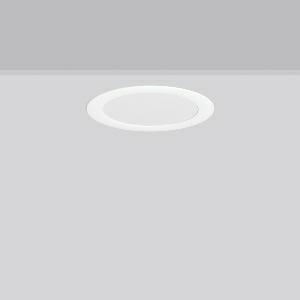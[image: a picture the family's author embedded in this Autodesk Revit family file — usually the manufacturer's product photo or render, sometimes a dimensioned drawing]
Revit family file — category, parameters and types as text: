
# Revit family: toledo_flat_round_e_672230_002_1_3b37
name_source: partatom
category: Lighting Fixtures
units: mm (PartAtom-declared; Revit-internal decimal feet)

## family parameters
Cut with Voids When Loaded = No
Host = Face
Light Source = No
Part Type = Normal
Room Calculation Point = No
Round Connector Dimension = Use Diameter
Shared = No

## types (1)
- TOLEDO FLAT round E (1 x LED Modul 840, 1800 lm, 4000)
    Apparent Load = 17 VA
    CIE Flux Codes = 48 79 96 100 100
    Color Rendering = 80
    Color Temperature = 4000
    Default Elevation = 1800 mm  [stored 5.90551 ft]
    Description = Series: TOLEDO FLAT round
Ultra thin recessed downlight. For escape route illumination. Housing: die-cast aluminium, powder-coated. Lightguide and diffuser made of non-yellowing plastic (PMMA). Diffuser opal matt plastic. Ceiling installation with spring system. Including separate LED converter with connecting cable 250 mm. Suitable for connection to central battery systems. External driver with simple plug-in locking system. 
Colour: white
Diameter: 255 mm
Height: 3 mm
Cut-out diameter: 234 mm
Recess height: 35 mm
Luminaire: recess height: 31-51 mm
Weight: 0.81 kg
Operating mode: maintained power mode
Lamp: LED
Socket: without socket
Colour temperature: 4000K
Colour rendering index (CRI): 80
System power: 17 W
Rated luminous flux: 1800 lm
Luminous flux, emergency: 1800 lm
System power, emergency: 17 W
Control gear: Regulated power supply
Protection class: II
Type of protection: IP 54
    Height = 0 mm  [stored 0 ft]
    Lamp = 1 x LED Modul 840
    Lamp Light Flux = 1800 lm
    Lamp count = 1
    Length = 255 mm
    Lifetime = 50000 h
    Luminous efficacy = 106 lm/W
    Manufacturer = RZB
    ModVariant = No
    Model = 672230.002.1
    Mounting Place = Ceiling
    Mounting Type = Recessed
    Number of Poles = 1
    OnlyDefault = Yes
    Power Factor = 1
    Product Name = TOLEDO FLAT round E
    Product group = Recessed downlights
    ProductGroupID = 402
    Protection Class = Protection class II
    Protection Degree = IP 40
    RLX_Detail_Level = 1
    RLX_Emergency_Light_Flux = 1800 lm
    RLX_Emergency_Type = 3
    RLX_Emergency_Type_DB = Yes
    RlxData = <blob elided: 30301 chars, md5=515a4622>
    Socket = socket
    Standby Power = 0 W
    System Light Flux = 1800 lm
    System Power = 17 W
    Type Comments = Product without accessories
    Type Image = 901453.002.jpg
    URL = http://relux.com
    VarID = ---
    Voltage = 230 V
    Voltage Range = 220-240 V
    Weight = 0.00 kg
    Width = 0 mm  [stored 0 ft]

note: [stored X ft] marks values corroborated as IEEE doubles in the binary element streams (Revit-internal decimal feet)

## geometry (parser evidence)
native form markers: Blend x4, Sweep x10
no freeform markers — native parametric forms only
